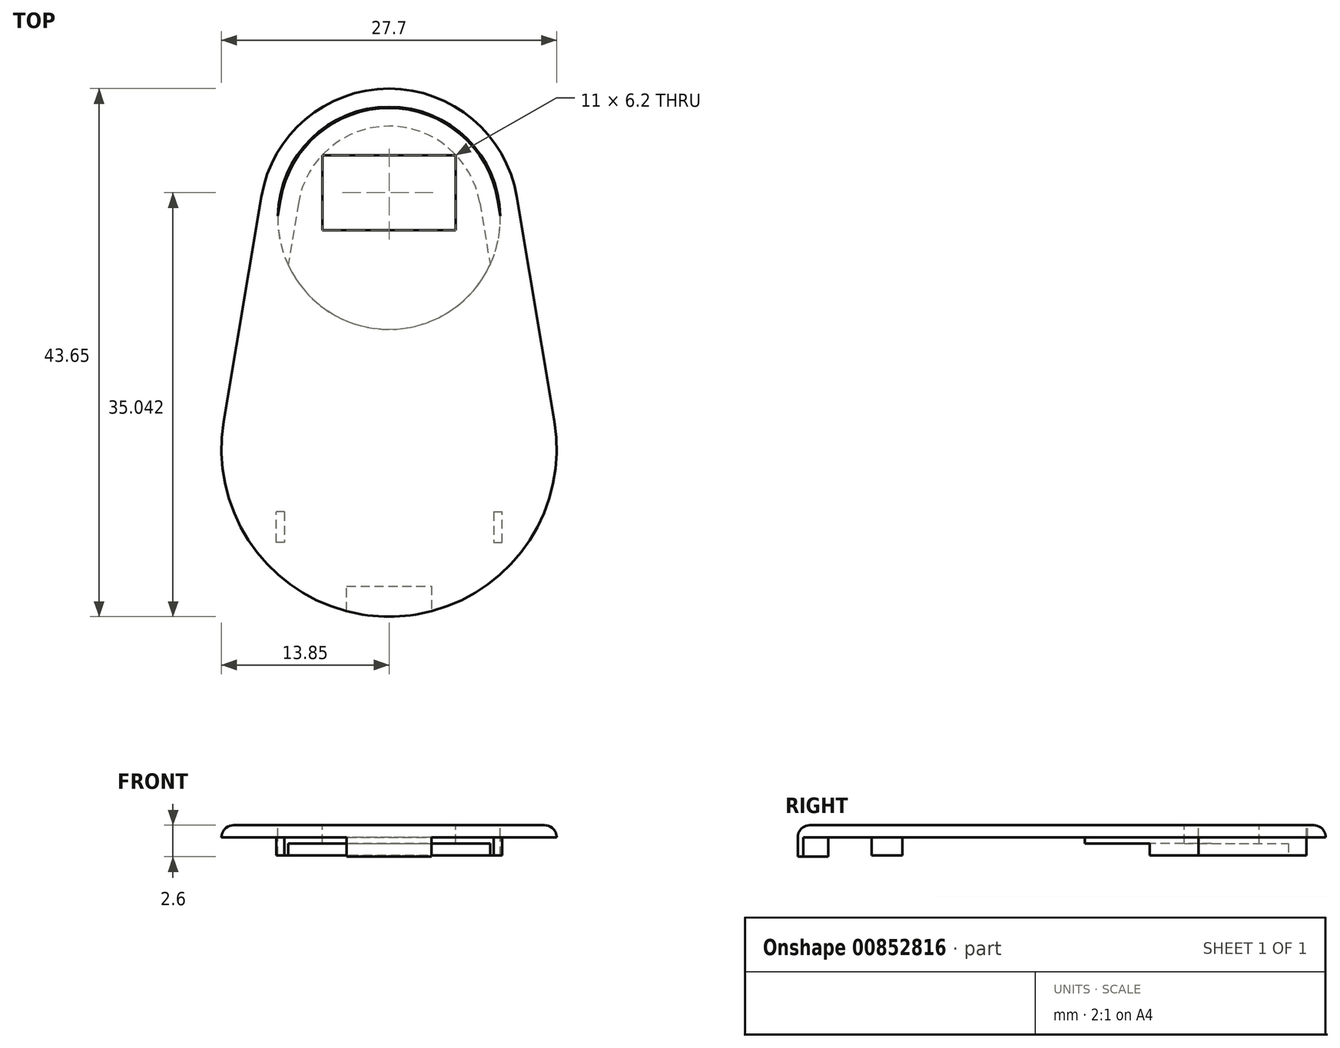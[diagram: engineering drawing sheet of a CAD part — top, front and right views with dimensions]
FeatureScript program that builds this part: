
annotation { "Feature Type Name" : "Feature", "Feature Type Description" : "" }
export const myFeature = defineFeature(function(context is Context, id is Id, definition is map)
    precondition{}
    {
        {
            var Q0;
            Q0=qCreatedBy(makeId("Top.planeOp"),FACE);
            var sketch = newSketch(context, id + "F0", { "sketchPlane" : qUnion([Q0])});
            skLineSegment(sketch, "E0", {"start": v(-8.01, 3.97) * mm, "end": v(8.01, 3.97) * mm});
            skArc(sketch, "E1", {"start": v(-8.01, 3.97) * mm, "mid": v(-10.75, 0.66) * mm, "end": v(-12.18, -3.4) * mm});
            skLineSegment(sketch, "E2", {"start": v(8.01, 3.97) * mm, "end": v(8.01, 3.97) * mm});
            skLineSegment(sketch, "E3", {"start": v(8.01, 9.14) * mm, "end": v(8.01, 9.14) * mm});
            skArc(sketch, "E4", {"start": v(-8.01, 3.97) * mm, "mid": v(-7.33, 6.56) * mm, "end": v(-8.01, 9.14) * mm});
            skLineSegment(sketch, "E5", {"start": v(-8.01, 9.14) * mm, "end": v(-8.01, 9.14) * mm});
            skArc(sketch, "E6", {"start": v(8.01, 9.14) * mm, "mid": v(7.33, 6.56) * mm, "end": v(8.01, 3.97) * mm});
            skArc(sketch, "E7", {"start": v(8.01, 9.14) * mm, "mid": v(8.01, 9.14) * mm, "end": v(8.01, 9.14) * mm});
            skArc(sketch, "E8", {"start": v(8.01, 9.14) * mm, "mid": v(9.06, 12.07) * mm, "end": v(9.07, 15.19) * mm});
            skArc(sketch, "E9", {"start": v(-8.01, 9.14) * mm, "mid": v(0, 4.47) * mm, "end": v(8.01, 9.14) * mm});
            skArc(sketch, "E10", {"start": v(-9.07, 15.19) * mm, "mid": v(-9.06, 12.07) * mm, "end": v(-8.01, 9.14) * mm});
            skLineSegment(sketch, "E11", {"start": v(-9.07, 15.19) * mm, "end": v(-9.07, 15.19) * mm});
            skArc(sketch, "E12", {"start": v(9.07, 15.19) * mm, "mid": v(0, 22.87) * mm, "end": v(-9.07, 15.19) * mm});
            skArc(sketch, "E13", {"start": v(12.18, -3.4) * mm, "mid": v(10.75, 0.66) * mm, "end": v(8.01, 3.97) * mm});
            skArc(sketch, "E14", {"start": v(-12.18, -3.4) * mm, "mid": v(0, -17.78) * mm, "end": v(12.18, -3.4) * mm});
            skLineSegment(sketch, "E15.0", {"start": v(-10.55, 15.43) * mm, "end": v(-13.66, -3.15) * mm});
            skArc(sketch, "E15.1", {"start": v(10.55, 15.43) * mm, "mid": v(0, 24.37) * mm, "end": v(-10.55, 15.43) * mm});
            skLineSegment(sketch, "E15.2", {"start": v(10.55, 15.43) * mm, "end": v(13.66, -3.15) * mm});
            skArc(sketch, "E15.3", {"start": v(-13.66, -3.15) * mm, "mid": v(0, -19.28) * mm, "end": v(13.66, -3.15) * mm});
            skPoint(sketch, "E16", {"position": v(12.35, -5.43) * mm});
            skPoint(sketch, "E17", {"position": v(-12.35, -5.43) * mm});
            skPoint(sketch, "E18", {"position": v(9, -5.43) * mm});
            skPoint(sketch, "E19", {"position": v(-9, -5.43) * mm});
            skLineSegment(sketch, "E20", {"start": v(0, -5.43) * mm, "end": v(0, -4.02) * mm});
            skLineSegment(sketch, "E21", {"start": v(0, -4.02) * mm, "end": v(0, -6.49) * mm});
            skSolve(sketch);
        }
        {
            var Q0;
            Q0=makeQuery(id+"F0.imprint","IMPRINT",FACE,{"disambiguationData":[TD([[makeQuery(id+"F0.imprint","IMPRINT",EDGE,{"derivedFrom":sQuery(id+"F0.wireOp",EDGE,"E1")}),-1.0]])]});
            var Q1;
            Q1=makeQuery(id+"F0.imprint","IMPRINT",FACE,{"disambiguationData":[TD([[makeQuery(id+"F0.imprint","IMPRINT",EDGE,{"derivedFrom":sQuery(id+"F0.wireOp",EDGE,"E0")}),-1.0]])]});
            var Q2;
            Q2=makeQuery(id+"F0.imprint","IMPRINT",FACE,{"disambiguationData":[TD([[makeQuery(id+"F0.imprint","IMPRINT",EDGE,{"derivedFrom":sQuery(id+"F0.wireOp",EDGE,"E0")}),1.0]])]});
            var Q3;
            Q3=makeQuery(id+"F0.imprint","IMPRINT",FACE,{"disambiguationData":[TD([[makeQuery(id+"F0.imprint","IMPRINT",EDGE,{"derivedFrom":sQuery(id+"F0.wireOp",EDGE,"E7")}),1.0]])]});
            extrude(context, id + "F1", {"entities" : qUnion([Q0, Q1, Q2, Q3]), "oppositeDirection" : true, "depth" : 1 * mm, "offsetDistance" : 25 * mm});
        }
        {
            var Q0;
            Q0=makeQuery(id+"F1.opExtrude","CAP_FACE",FACE,{"disambiguationData":[OSD([sQuery(id+"F0.wireOp",EDGE,"E15.0"),sQuery(id+"F0.wireOp",EDGE,"E15.1"),sQuery(id+"F0.wireOp",EDGE,"E15.2"),sQuery(id+"F0.wireOp",EDGE,"E15.3")])],"isStart":true});
            var sketch = newSketch(context, id + "F2", { "sketchPlane" : qUnion([Q0])});
            skLineSegment(sketch, "E22.bottom", {"start": v(-8.65, 11.24) * mm, "end": v(8.65, 11.24) * mm, "construction": true});
            skLineSegment(sketch, "E22.top", {"start": v(-5.65, -16.76) * mm, "end": v(5.65, -16.76) * mm, "construction": true});
            skLineSegment(sketch, "E22.left", {"start": v(-8.65, 11.24) * mm, "end": v(-8.65, -13.76) * mm});
            skLineSegment(sketch, "E22.right", {"start": v(8.65, 11.24) * mm, "end": v(8.65, -13.76) * mm});
            skPoint(sketch, "E23", {"position": v(0, -16.76) * mm});
            skLineSegment(sketch, "E24.bottom", {"start": v(-3.5, -16.76) * mm, "end": v(3.5, -16.76) * mm});
            skLineSegment(sketch, "E24.top", {"start": v(-3.5, -17.96) * mm, "end": v(3.5, -17.96) * mm});
            skLineSegment(sketch, "E24.left", {"start": v(-3.5, -16.76) * mm, "end": v(-3.5, -17.96) * mm});
            skLineSegment(sketch, "E24.right", {"start": v(3.5, -16.76) * mm, "end": v(3.5, -17.96) * mm});
            skLineSegment(sketch, "E25", {"start": v(-3.5, -17.96) * mm, "end": v(-3.5, -19.56) * mm, "construction": true});
            skLineSegment(sketch, "E26", {"start": v(-3.5, -19.56) * mm, "end": v(3.5, -19.56) * mm, "construction": true});
            skLineSegment(sketch, "E27", {"start": v(3.5, -19.56) * mm, "end": v(3.5, -17.96) * mm, "construction": true});
            skPoint(sketch, "E28.visualSharp", {"position": v(-8.65, -16.76) * mm});
            skArc(sketch, "E28.filletArc", {"start": v(-8.65, -13.76) * mm, "mid": v(-8.64, -14.03) * mm, "end": v(-8.6, -14.3) * mm});
            skPoint(sketch, "E29.visualSharp", {"position": v(8.65, -16.76) * mm});
            skArc(sketch, "E29.filletArc", {"start": v(5.65, -16.76) * mm, "mid": v(7.57, -16.06) * mm, "end": v(8.6, -14.3) * mm, "construction": true});
            skLineSegment(sketch, "E30.0", {"start": v(-9.07, 15.19) * mm, "end": v(-12.18, -3.4) * mm, "construction": true});
            skArc(sketch, "E30.1", {"start": v(9.07, 15.19) * mm, "mid": v(0, 22.87) * mm, "end": v(-9.07, 15.19) * mm, "construction": true});
            skLineSegment(sketch, "E30.2", {"start": v(9.07, 15.19) * mm, "end": v(12.18, -3.4) * mm, "construction": true});
            skArc(sketch, "E30.3", {"start": v(-12.18, -3.4) * mm, "mid": v(-11.73, -9.28) * mm, "end": v(-8.6, -14.3) * mm, "construction": true});
            skArc(sketch, "E31", {"start": v(8.6, -14.3) * mm, "mid": v(11.73, -9.28) * mm, "end": v(12.18, -3.4) * mm, "construction": true});
            skLineSegment(sketch, "E32", {"start": v(3.5, -17.96) * mm, "end": v(3.5, -19.56) * mm});
            skLineSegment(sketch, "E33", {"start": v(-3.5, -19.56) * mm, "end": v(-3.5, -17.96) * mm});
            skLineSegment(sketch, "E34", {"start": v(3.5, -19.56) * mm, "end": v(-3.5, -19.56) * mm});
            skLineSegment(sketch, "E35.bottom", {"start": v(-8.65, 11.24) * mm, "end": v(-9.48, 11.24) * mm});
            skLineSegment(sketch, "E35.top", {"start": v(-8.65, 7.46) * mm, "end": v(-9.48, 7.46) * mm});
            skLineSegment(sketch, "E35.left", {"start": v(-8.65, 11.24) * mm, "end": v(-8.65, 7.46) * mm});
            skLineSegment(sketch, "E35.right", {"start": v(-9.48, 11.24) * mm, "end": v(-9.48, 7.46) * mm});
            skPoint(sketch, "E36.oppositeSnap0", {"position": v(-9.07, 7.46) * mm});
            skLineSegment(sketch, "E36.bottom", {"start": v(8.65, 11.24) * mm, "end": v(9.43, 11.24) * mm});
            skLineSegment(sketch, "E36.top", {"start": v(8.65, 7.46) * mm, "end": v(9.43, 7.46) * mm});
            skLineSegment(sketch, "E36.left", {"start": v(8.65, 11.24) * mm, "end": v(8.65, 7.46) * mm});
            skLineSegment(sketch, "E36.right", {"start": v(9.43, 11.24) * mm, "end": v(9.43, 7.46) * mm});
            skLineSegment(sketch, "E37.bottom", {"start": v(-8.65, -13.16) * mm, "end": v(-9.3, -13.16) * mm});
            skLineSegment(sketch, "E37.top", {"start": v(-8.65, -10.62) * mm, "end": v(-9.3, -10.62) * mm});
            skLineSegment(sketch, "E37.left", {"start": v(-8.65, -13.16) * mm, "end": v(-8.65, -10.62) * mm});
            skLineSegment(sketch, "E37.right", {"start": v(-9.3, -13.16) * mm, "end": v(-9.3, -10.62) * mm});
            skLineSegment(sketch, "E38.bottom", {"start": v(8.65, -13.16) * mm, "end": v(9.35, -13.16) * mm});
            skLineSegment(sketch, "E38.top", {"start": v(8.65, -10.62) * mm, "end": v(9.35, -10.62) * mm});
            skLineSegment(sketch, "E38.left", {"start": v(8.65, -13.16) * mm, "end": v(8.65, -10.62) * mm});
            skLineSegment(sketch, "E38.right", {"start": v(9.35, -13.16) * mm, "end": v(9.35, -10.62) * mm});
            skArc(sketch, "E39", {"start": v(-8.6, -14.3) * mm, "mid": v(-7.57, -16.06) * mm, "end": v(-5.65, -16.76) * mm, "construction": true});
            skArc(sketch, "E40", {"start": v(8.6, -14.3) * mm, "mid": v(8.64, -14.03) * mm, "end": v(8.65, -13.76) * mm});
            skLineSegment(sketch, "E41.0", {"start": v(8.98, 15.17) * mm, "end": v(12.08, -3.41) * mm});
            skArc(sketch, "E41.1", {"start": v(8.5, -14.24) * mm, "mid": v(11.63, -9.27) * mm, "end": v(12.08, -3.41) * mm});
            skArc(sketch, "E41.2", {"start": v(8.98, 15.17) * mm, "mid": v(0, 22.77) * mm, "end": v(-8.98, 15.17) * mm});
            skArc(sketch, "E41.3", {"start": v(5.65, -16.66) * mm, "mid": v(7.52, -15.97) * mm, "end": v(8.5, -14.24) * mm});
            skLineSegment(sketch, "E41.4", {"start": v(-8.98, 15.17) * mm, "end": v(-12.08, -3.41) * mm});
            skArc(sketch, "E41.5", {"start": v(-12.08, -3.41) * mm, "mid": v(-11.63, -9.27) * mm, "end": v(-8.5, -14.24) * mm});
            skArc(sketch, "E41.6", {"start": v(-8.5, -14.24) * mm, "mid": v(-7.52, -15.97) * mm, "end": v(-5.65, -16.66) * mm});
            skLineSegment(sketch, "E41.7", {"start": v(-5.65, -16.66) * mm, "end": v(5.65, -16.66) * mm});
            skSolve(sketch);
        }
        {
            var Q0;
            Q0=makeQuery(id+"F2.imprint","IMPRINT",FACE,{"disambiguationData":[TD([[makeQuery(id+"F2.imprint","IMPRINT",EDGE,{"derivedFrom":sQuery(id+"F2.wireOp",EDGE,"E38.bottom")}),1.0]])]});
            var Q1;
            Q1=makeQuery(id+"F2.imprint","IMPRINT",FACE,{"disambiguationData":[TD([[makeQuery(id+"F2.imprint","IMPRINT",EDGE,{"derivedFrom":sQuery(id+"F2.wireOp",EDGE,"E37.bottom")}),-1.0]])]});
            var Q2;
            Q2=makeQuery(id+"F2.imprint","IMPRINT",FACE,{"disambiguationData":[TD([[makeQuery(id+"F2.imprint","IMPRINT",EDGE,{"derivedFrom":sQuery(id+"F2.wireOp",EDGE,"E35.bottom")}),-1.0]])]});
            var Q3;
            Q3=makeQuery(id+"F2.imprint","IMPRINT",FACE,{"disambiguationData":[TD([[makeQuery(id+"F2.imprint","IMPRINT",EDGE,{"derivedFrom":sQuery(id+"F2.wireOp",EDGE,"E36.bottom")}),-1.0]])]});
            var Q4;
            Q4=makeQuery(id+"F2.imprint","IMPRINT",FACE,{"disambiguationData":[TD([[makeQuery(id+"F2.imprint","IMPRINT",EDGE,{"derivedFrom":sQuery(id+"F2.wireOp",EDGE,"E35.bottom")}),1.0]])]});
            extrude(context, id + "F3", {"entities" : qUnion([Q0, Q1, Q2, Q3, Q4]), "operationType" : NewBodyOperationType.ADD, "oppositeDirection" : true, "depth" : 2.5 * mm, "offsetDistance" : 25 * mm});
        }
        {
            var Q0;
            {var subQ0=sQuery(id+"F2.wireOp",EDGE,"E24.top");Q0=makeQuery(id+"F2.imprint","IMPRINT",FACE,{"disambiguationData":[TD([[makeQuery(id+"F2.imprint","IMPRINT",EDGE,{"derivedFrom":subQ0}),-1.0]])]});}
            var Q1;
            Q1=makeQuery(id+"F2.imprint","IMPRINT",FACE,{"disambiguationData":[TD([[makeQuery(id+"F2.imprint","IMPRINT",EDGE,{"derivedFrom":sQuery(id+"F2.wireOp",EDGE,"E24.bottom")}),-1.0]])]});
            extrude(context, id + "F4", {"entities" : qUnion([Q0, Q1]), "operationType" : NewBodyOperationType.ADD, "oppositeDirection" : true, "depth" : 2.6 * mm, "offsetDistance" : 25 * mm});
        }
        {
            var Q0;
            Q0=makeQuery(id+"F3.opExtrude","CAP_FACE",FACE,{"disambiguationData":[OSD([sQuery(id+"F2.wireOp",EDGE,"E41.0"),sQuery(id+"F2.wireOp",EDGE,"E41.1"),sQuery(id+"F2.wireOp",EDGE,"E41.2"),sQuery(id+"F2.wireOp",EDGE,"E41.3"),sQuery(id+"F2.wireOp",EDGE,"E41.4"),sQuery(id+"F2.wireOp",EDGE,"E41.5"),sQuery(id+"F2.wireOp",EDGE,"E41.6"),sQuery(id+"F2.wireOp",EDGE,"E41.7")])],"isStart":false});
            var sketch = newSketch(context, id + "F5", { "sketchPlane" : qUnion([Q0])});
            skLineSegment(sketch, "E42.0", {"start": v(-7.5, -14.92) * mm, "end": v(-10.6, 3.66) * mm});
            skArc(sketch, "E42.1", {"start": v(7.5, -14.92) * mm, "mid": v(0, -21.27) * mm, "end": v(-7.5, -14.92) * mm});
            skArc(sketch, "E42.2", {"start": v(-10.6, 3.66) * mm, "mid": v(-10.11, 9.07) * mm, "end": v(-7.04, 13.56) * mm});
            skLineSegment(sketch, "E42.3", {"start": v(7.5, -14.92) * mm, "end": v(10.6, 3.66) * mm});
            skArc(sketch, "E42.4", {"start": v(-7.04, 13.56) * mm, "mid": v(-6.7, 14.67) * mm, "end": v(-5.65, 15.16) * mm});
            skLineSegment(sketch, "E42.5", {"start": v(-5.65, 15.16) * mm, "end": v(5.65, 15.16) * mm});
            skArc(sketch, "E42.6", {"start": v(5.65, 15.16) * mm, "mid": v(6.7, 14.67) * mm, "end": v(7.04, 13.56) * mm});
            skArc(sketch, "E42.7", {"start": v(7.04, 13.56) * mm, "mid": v(10.11, 9.07) * mm, "end": v(10.6, 3.66) * mm});
            skSolve(sketch);
        }
        {
            var Q0;
            Q0=makeQuery(id+"F5.imprint","IMPRINT",FACE,{"disambiguationData":[TD([[makeQuery(id+"F5.imprint","IMPRINT",EDGE,{"derivedFrom":sQuery(id+"F5.wireOp",EDGE,"E42.0")}),-1.0]])]});
            extrude(context, id + "F6", {"entities" : qUnion([Q0]), "operationType" : NewBodyOperationType.REMOVE, "oppositeDirection" : true, "depth" : 1 * mm, "offsetDistance" : 25 * mm});
        }
        {
            var Q0;
            Q0=makeQuery(id+"F1.opExtrude","CAP_EDGE",EDGE,{"disambiguationData":[OSD([sQuery(id+"F0.wireOp",EDGE,"E15.3")])],"isStart":true});
            var Q1;
            Q1=makeQuery(id+"F1.opExtrude","CAP_EDGE",EDGE,{"disambiguationData":[OSD([sQuery(id+"F0.wireOp",EDGE,"E15.1")])],"isStart":true});
            var Q2;
            Q2=makeQuery(id+"F1.opExtrude","CAP_EDGE",EDGE,{"disambiguationData":[OSD([sQuery(id+"F0.wireOp",EDGE,"E15.2")])],"isStart":true});
            var Q3;
            Q3=makeQuery(id+"F1.opExtrude","CAP_EDGE",EDGE,{"disambiguationData":[OSD([sQuery(id+"F0.wireOp",EDGE,"E15.0")])],"isStart":true});
            fillet(context, id + "F7", {"entities" : qUnion([Q0, Q1, Q2, Q3]), "radius" : 1 * mm, "tangentPropagation" : true, "allowEdgeOverflow" : false});
        }
        {
            var Q0;
            Q0=makeQuery(id+"F1.opExtrude","CAP_FACE",FACE,{"disambiguationData":[OSD([sQuery(id+"F0.wireOp",EDGE,"E15.0"),sQuery(id+"F0.wireOp",EDGE,"E15.1"),sQuery(id+"F0.wireOp",EDGE,"E15.2"),sQuery(id+"F0.wireOp",EDGE,"E15.3")])],"isStart":true});
            var sketch = newSketch(context, id + "F8", { "sketchPlane" : qUnion([Q0])});
            skLineSegment(sketch, "E43.bottom", {"start": v(-5.5, 18.86) * mm, "end": v(5.5, 18.86) * mm});
            skLineSegment(sketch, "E43.top", {"start": v(-5.5, 12.66) * mm, "end": v(5.5, 12.66) * mm});
            skLineSegment(sketch, "E43.left", {"start": v(-5.5, 18.86) * mm, "end": v(-5.5, 12.66) * mm});
            skLineSegment(sketch, "E43.right", {"start": v(5.5, 18.86) * mm, "end": v(5.5, 12.66) * mm});
            skPoint(sketch, "E44", {"position": v(0, 5.97) * mm});
            skPoint(sketch, "E44.positionSnap0", {"position": v(0, 23.37) * mm});
            skPoint(sketch, "E45", {"position": v(0, 18.86) * mm});
            skLineSegment(sketch, "E46", {"start": v(-5.5, 18.86) * mm, "end": v(-10, 18.86) * mm, "construction": true});
            skLineSegment(sketch, "E47", {"start": v(-5.5, 12.66) * mm, "end": v(-10, 12.66) * mm, "construction": true});
            skLineSegment(sketch, "E48", {"start": v(-10, 12.66) * mm, "end": v(-10, 18.86) * mm, "construction": true});
            skLineSegment(sketch, "E49", {"start": v(5.5, 18.86) * mm, "end": v(10, 18.86) * mm, "construction": true});
            skLineSegment(sketch, "E50", {"start": v(10, 18.86) * mm, "end": v(10, 12.66) * mm, "construction": true});
            skLineSegment(sketch, "E51", {"start": v(10, 12.66) * mm, "end": v(5.5, 12.66) * mm, "construction": true});
            skSolve(sketch);
        }
        {
            var Q0;
            Q0=makeQuery(id+"F8.imprint","IMPRINT",FACE,{"disambiguationData":[TD([[makeQuery(id+"F8.imprint","IMPRINT",EDGE,{"derivedFrom":sQuery(id+"F8.wireOp",EDGE,"E43.bottom")}),-1.0]])]});
            extrude(context, id + "F9", {"entities" : qUnion([Q0]), "operationType" : NewBodyOperationType.REMOVE, "oppositeDirection" : true, "depth" : 6 * mm, "offsetDistance" : 25 * mm});
        }
    });
